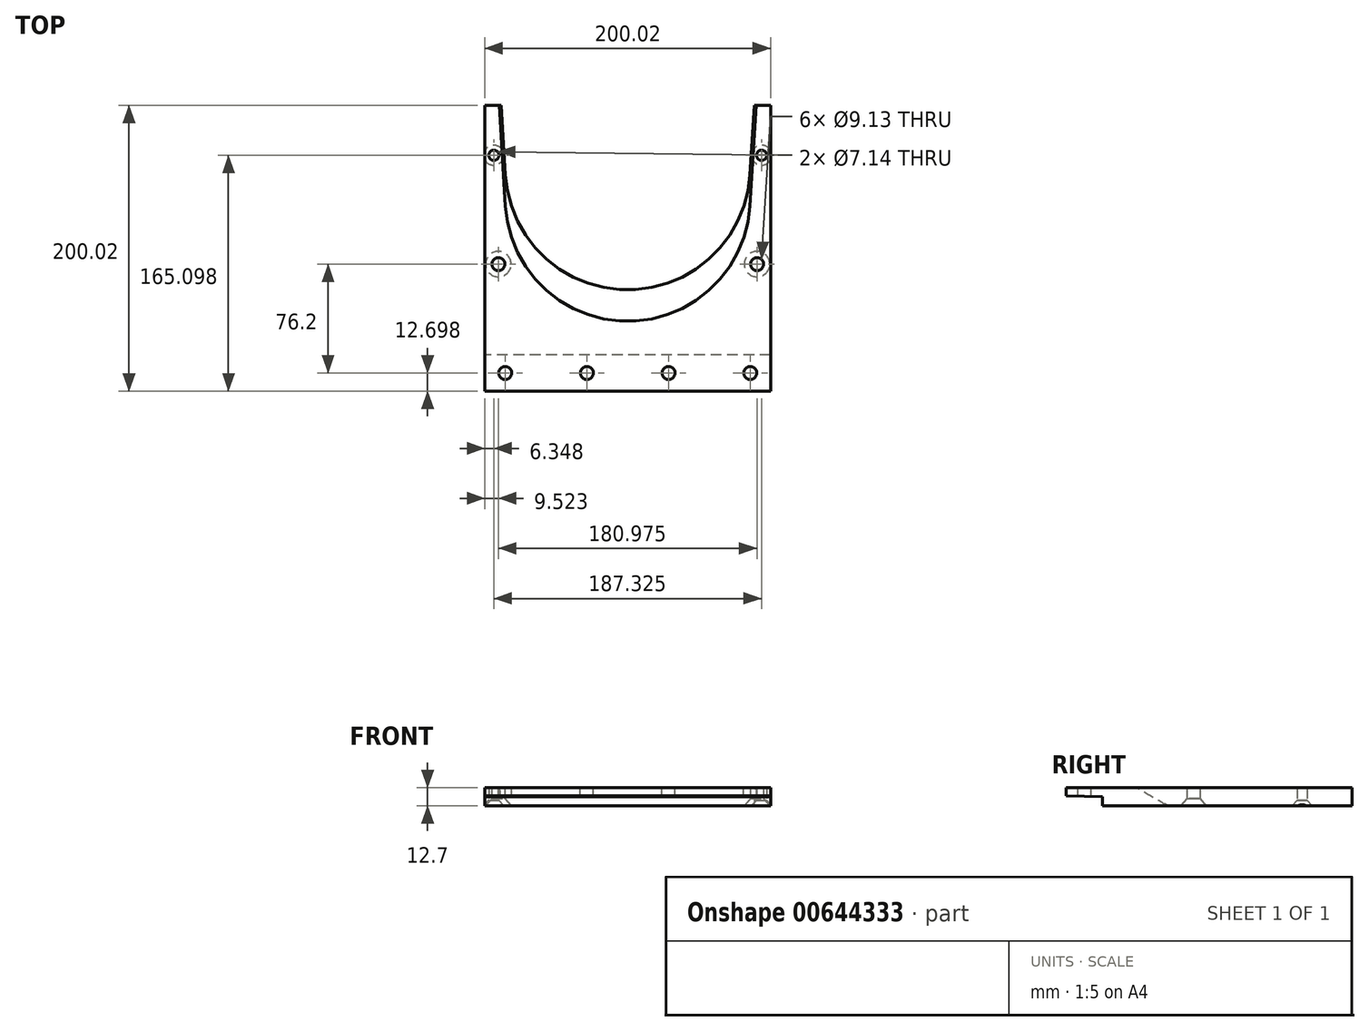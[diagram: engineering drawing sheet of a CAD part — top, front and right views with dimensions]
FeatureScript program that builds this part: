
annotation { "Feature Type Name" : "Feature", "Feature Type Description" : "" }
export const myFeature = defineFeature(function(context is Context, id is Id, definition is map)
    precondition{}
    {
        {
            var Q0;
            Q0=qCreatedBy(makeId("Top.planeOp"),FACE);
            var sketch = newSketch(context, id + "F0", { "sketchPlane" : qUnion([Q0])});
            skLineSegment(sketch, "E0.bottom", {"start": v(100.01, 100.01) * mm, "end": v(-100.01, 100.01) * mm});
            skLineSegment(sketch, "E0.top", {"start": v(100.01, -100.01) * mm, "end": v(-100.01, -100.01) * mm});
            skLineSegment(sketch, "E0.left", {"start": v(100.01, 100.01) * mm, "end": v(100.01, -100.01) * mm});
            skLineSegment(sketch, "E0.right", {"start": v(-100.01, 100.01) * mm, "end": v(-100.01, -100.01) * mm});
            skPoint(sketch, "E0.middle", {"position": v(0, 0) * mm});
            skSolve(sketch);
        }
        {
            var Q0;
            Q0=makeQuery(id+"F0.imprint","IMPRINT",FACE,{"disambiguationData":[TD([[makeQuery(id+"F0.imprint","IMPRINT",EDGE,{"derivedFrom":sQuery(id+"F0.wireOp",EDGE,"E0.bottom")}),1.0]])]});
            extrude(context, id + "F1", {"entities" : qUnion([Q0]), "depth" : 12.7 * mm, "offsetDistance" : 25.4 * mm});
        }
        {
            var Q0;
            Q0=makeQuery(id+"F1.opExtrude","CAP_FACE",FACE,{"disambiguationData":[OSD([sQuery(id+"F0.wireOp",EDGE,"E0.bottom"),sQuery(id+"F0.wireOp",EDGE,"E0.top"),sQuery(id+"F0.wireOp",EDGE,"E0.left"),sQuery(id+"F0.wireOp",EDGE,"E0.right")])],"isStart":false});
            var sketch = newSketch(context, id + "F2", { "sketchPlane" : qUnion([Q0])});
            skLineSegment(sketch, "E1", {"start": v(-100.01, -51.1) * mm, "end": v(100.01, -51.1) * mm});
            skSolve(sketch);
        }
        {
            var Q0;
            Q0=makeQuery(id+"F1.opExtrude","SWEPT_FACE",FACE,{"disambiguationData":[OSD([sQuery(id+"F0.wireOp",EDGE,"E0.right")])]});
            var sketch = newSketch(context, id + "F3", { "sketchPlane" : qUnion([Q0])});
            skLineSegment(sketch, "E2", {"start": v(100.01, 7.11) * mm, "end": v(74.61, 6.23) * mm});
            skLineSegment(sketch, "E3", {"start": v(74.61, 6.23) * mm, "end": v(74.61, 0) * mm});
            skLineSegment(sketch, "E4", {"start": v(74.61, 0) * mm, "end": v(100.01, 0) * mm});
            skLineSegment(sketch, "E5", {"start": v(100.01, 0) * mm, "end": v(100.01, 7.11) * mm});
            skSolve(sketch);
        }
        {
            var Q0;
            Q0 = qSketchRegion(id + "F3", true);
            extrude(context, id + "F4", {"entities" : qUnion([Q0]), "operationType" : NewBodyOperationType.REMOVE, "oppositeDirection" : true, "depth" : 230.89 * mm, "offsetDistance" : 25.4 * mm});
        }
        {
            var Q0;
            {var subQ0=sQuery(id+"F2.wireOp",EDGE,"E1");Q0=makeQuery(id+"F2.imprint","IMPRINT",FACE,{"disambiguationData":[TD([[makeQuery(id+"F2.imprint","IMPRINT",EDGE,{"derivedFrom":subQ0}),-1.0]])]});}
            var sketch = newSketch(context, id + "F5", { "sketchPlane" : qUnion([Q0])});
            skCircle(sketch, "E6", {"center": v(-85.73, -87.31) * mm, "radius": 4.56 * mm});
            skCircle(sketch, "E7", {"center": v(-28.58, -87.31) * mm, "radius": 4.56 * mm});
            skCircle(sketch, "E8", {"center": v(28.58, -87.31) * mm, "radius": 4.56 * mm});
            skCircle(sketch, "E9", {"center": v(85.73, -87.31) * mm, "radius": 4.56 * mm});
            skSolve(sketch);
        }
        {
            var Q0;
            Q0 = qSketchRegion(id + "F5", true);
            extrude(context, id + "F6", {"entities" : qUnion([Q0]), "operationType" : NewBodyOperationType.REMOVE, "oppositeDirection" : true, "depth" : 25.4 * mm, "offsetDistance" : 25.4 * mm});
        }
        {
            var Q0;
            Q0=makeQuery(id+"F1.opExtrude","CAP_FACE",FACE,{"disambiguationData":[OSD([sQuery(id+"F0.wireOp",EDGE,"E0.bottom"),sQuery(id+"F0.wireOp",EDGE,"E0.top"),sQuery(id+"F0.wireOp",EDGE,"E0.left"),sQuery(id+"F0.wireOp",EDGE,"E0.right")])],"isStart":true});
            var sketch = newSketch(context, id + "F7", { "sketchPlane" : qUnion([Q0])});
            skPoint(sketch, "E10", {"position": v(90.49, 11.11) * mm});
            skPoint(sketch, "E11", {"position": v(93.66, -65.09) * mm});
            skPoint(sketch, "E12", {"position": v(-93.66, -65.09) * mm});
            skPoint(sketch, "E13", {"position": v(-90.49, 11.11) * mm});
            skSolve(sketch);
        }
        {
            var Q0;
            Q0=sQuery(id+"F7.wireOp",VERTEX,"E10");
            var Q1;
            Q1=sQuery(id+"F7.wireOp",VERTEX,"E13");
            var Q2;
            Q2=makeQuery(id+"F1.opExtrude","SWEPT_BODY",BODY,{"disambiguationData":[OSD([sQuery(id+"F0.wireOp",EDGE,"E0.bottom"),sQuery(id+"F0.wireOp",EDGE,"E0.top"),sQuery(id+"F0.wireOp",EDGE,"E0.left"),sQuery(id+"F0.wireOp",EDGE,"E0.right")])]});
            hole(context, id + "F8", {"style" : HoleStyle.C_SINK, "endStyle" : HoleEndStyle.THROUGH, "holeDiameter" : 9.13 * mm, "cSinkDiameter" : 17.78 * mm, "cSinkAngle" : 82 * degree, "majorDiameter" : 6.35 * mm, "isTappedThrough" : true, "tappedDepth" : 12.7 * mm, "tapClearance" : 3, "locations" : qUnion([Q0, Q1]), "scope" : qUnion([Q2])});
        }
        {
            var Q0;
            Q0=sQuery(id+"F7.wireOp",VERTEX,"E11");
            var Q1;
            Q1=sQuery(id+"F7.wireOp",VERTEX,"E12");
            var Q2;
            Q2=makeQuery(id+"F1.opExtrude","SWEPT_BODY",BODY,{"disambiguationData":[OSD([sQuery(id+"F0.wireOp",EDGE,"E0.bottom"),sQuery(id+"F0.wireOp",EDGE,"E0.top"),sQuery(id+"F0.wireOp",EDGE,"E0.left"),sQuery(id+"F0.wireOp",EDGE,"E0.right")])]});
            hole(context, id + "F9", {"style" : HoleStyle.C_SINK, "endStyle" : HoleEndStyle.THROUGH, "holeDiameter" : 7.14 * mm, "cSinkDiameter" : 13.97 * mm, "cSinkAngle" : 82 * degree, "majorDiameter" : 6.35 * mm, "isTappedThrough" : true, "tappedDepth" : 12.7 * mm, "tapClearance" : 3, "locations" : qUnion([Q0, Q1]), "scope" : qUnion([Q2])});
        }
        {
            var Q0;
            {var subQ0=sQuery(id+"F2.wireOp",EDGE,"E1");Q0=makeQuery(id+"F2.imprint","IMPRINT",FACE,{"disambiguationData":[TD([[makeQuery(id+"F2.imprint","IMPRINT",EDGE,{"derivedFrom":subQ0}),1.0]])]});}
            var sketch = newSketch(context, id + "F10", { "sketchPlane" : qUnion([Q0])});
            skLineSegment(sketch, "E14", {"start": v(89.79, 100.01) * mm, "end": v(85.57, 29.51) * mm});
            skLineSegment(sketch, "E15", {"start": v(-89.79, 100.01) * mm, "end": v(-85.57, 29.51) * mm});
            skArc(sketch, "E16", {"start": v(-85.57, 29.51) * mm, "mid": v(0, -51.1) * mm, "end": v(85.57, 29.51) * mm});
            skPoint(sketch, "E17", {"position": v(0, -51.1) * mm});
            skLineSegment(sketch, "E18", {"start": v(89.79, 100.01) * mm, "end": v(-89.79, 100.01) * mm});
            skSolve(sketch);
        }
        {
            var Q0;
            Q0=qCreatedBy(makeId("Right.planeOp"),FACE);
            var sketch = newSketch(context, id + "F11", { "sketchPlane" : qUnion([Q0])});
            skLineSegment(sketch, "E19", {"start": v(113.89, -82.55) * mm, "end": v(-216.07, 107.95) * mm});
            skSolve(sketch);
        }
        {
            var Q0;
            Q0 = qSketchRegion(id + "F10", true);
            var Q1;
            Q1 = qConstructionFilter(qBodyType(qCreatedBy(id + "F11" ,EDGE), BodyType.WIRE), ConstructionObject.NO);
            sweep(context, id + "F12", {"operationType" : NewBodyOperationType.REMOVE, "profiles" : qUnion([Q0]), "path" : qUnion([Q1])});
        }
    });
